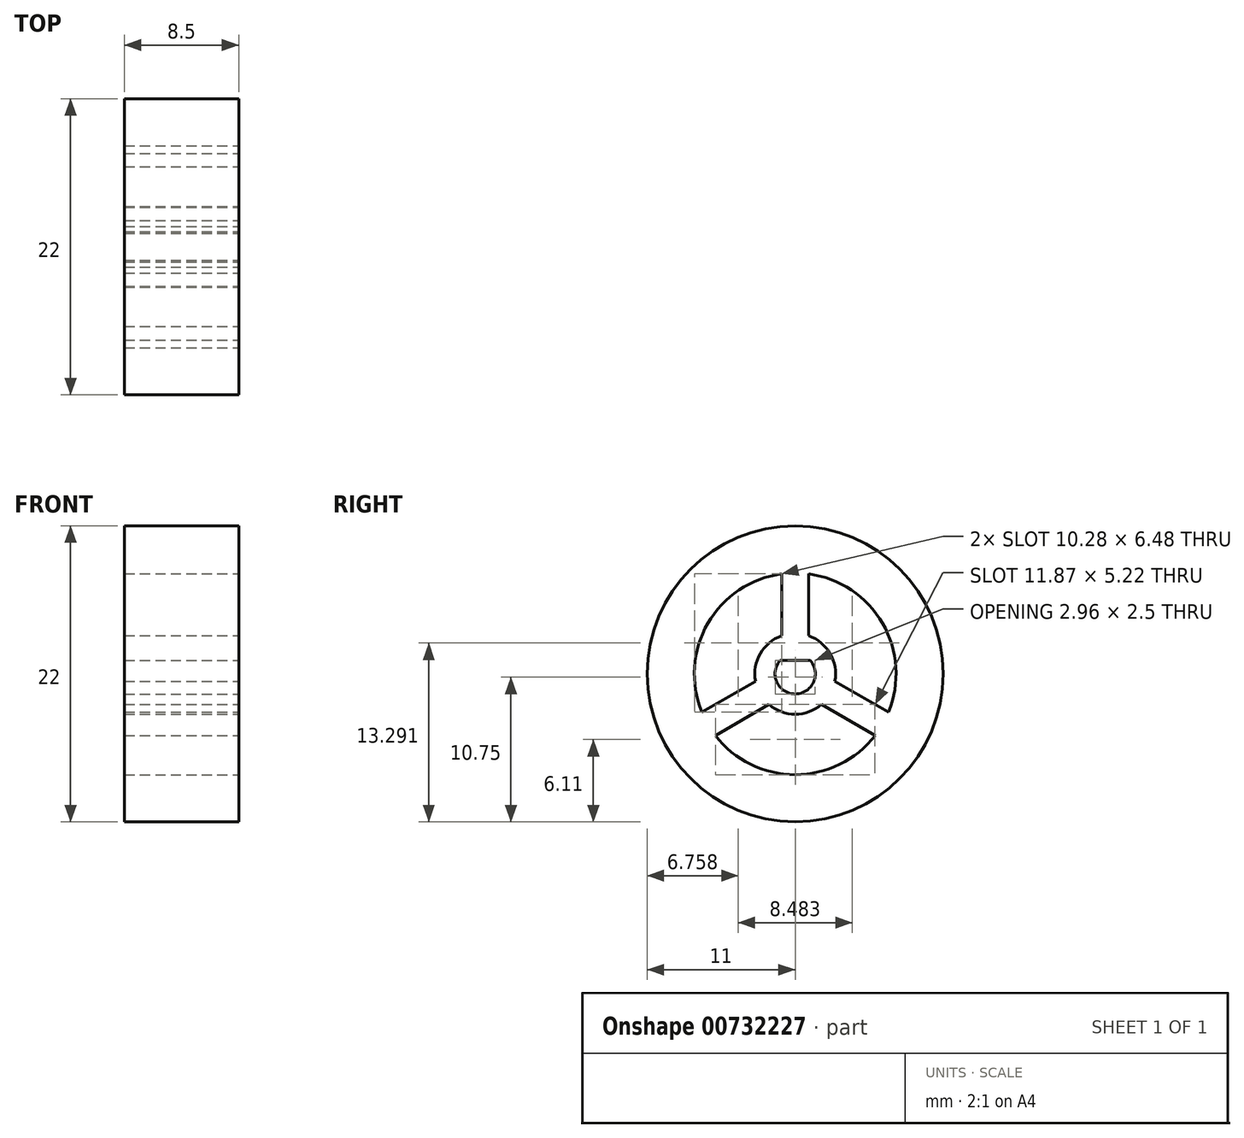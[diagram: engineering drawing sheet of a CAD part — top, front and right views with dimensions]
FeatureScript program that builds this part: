
annotation { "Feature Type Name" : "Feature", "Feature Type Description" : "" }
export const myFeature = defineFeature(function(context is Context, id is Id, definition is map)
    precondition{}
    {
        {
            var Q0;
            Q0=qCreatedBy(makeId("Right.planeOp"),FACE);
            var sketch = newSketch(context, id + "F0", { "sketchPlane" : qUnion([Q0])});
            skCircle(sketch, "E0", {"center": v(0, 0) * mm, "radius": 11 * mm});
            skSolve(sketch);
        }
        {
            var Q0;
            Q0 = qSketchRegion(id + "F0", true);
            extrude(context, id + "F1", {"entities" : qUnion([Q0]), "depth" : 8.5 * mm, "offsetDistance" : 25 * mm});
        }
        {
            var Q0;
            Q0=makeQuery(id+"F1.opExtrude","CAP_FACE",FACE,{"disambiguationData":[OSD([sQuery(id+"F0.wireOp",EDGE,"E0")])],"isStart":false});
            var sketch = newSketch(context, id + "F2", { "sketchPlane" : qUnion([Q0])});
            skArc(sketch, "E1", {"start": v(-1, 7.43) * mm, "mid": v(-6.5, 3.75) * mm, "end": v(-6.94, -2.85) * mm});
            skArc(sketch, "E2", {"start": v(-1, 2.83) * mm, "mid": v(-2.6, 1.5) * mm, "end": v(-2.95, -0.55) * mm});
            skLineSegment(sketch, "E3", {"start": v(0, 7.5) * mm, "end": v(0, 3) * mm, "construction": true});
            skLineSegment(sketch, "E4", {"start": v(0, 3) * mm, "end": v(1, 3) * mm, "construction": true});
            skLineSegment(sketch, "E5", {"start": v(1, 3) * mm, "end": v(1, 7.43) * mm});
            skLineSegment(sketch, "E6", {"start": v(1, 3) * mm, "end": v(1, 2.83) * mm});
            skLineSegment(sketch, "E7.MirrorCS", {"start": v(1, 3) * mm, "end": v(1, 3.17) * mm});
            skLineSegment(sketch, "E8.MirrorCS", {"start": v(1, 3) * mm, "end": v(1, -1.43) * mm});
            skLineSegment(sketch, "E9.MirrorCS", {"start": v(-1, 3) * mm, "end": v(-1, 7.43) * mm});
            skLineSegment(sketch, "E10.MirrorCS", {"start": v(0, 3) * mm, "end": v(-1, 3) * mm, "construction": true});
            skLineSegment(sketch, "E11.MirrorCS", {"start": v(-1, 3) * mm, "end": v(-1, 2.83) * mm});
            skLineSegment(sketch, "E12.1.0", {"start": v(-2.1, -2.37) * mm, "end": v(-5.94, -4.58) * mm});
            skLineSegment(sketch, "E12.1.1", {"start": v(-6.5, -3.75) * mm, "end": v(-2.6, -1.5) * mm, "construction": true});
            skLineSegment(sketch, "E12.1.2", {"start": v(-3.1, -0.63) * mm, "end": v(-6.94, -2.85) * mm});
            skLineSegment(sketch, "E12.1.3", {"start": v(-2.6, -1.5) * mm, "end": v(-3.1, -0.63) * mm, "construction": true});
            skLineSegment(sketch, "E12.1.4", {"start": v(-3.1, -0.63) * mm, "end": v(-2.95, -0.55) * mm});
            skLineSegment(sketch, "E12.1.5", {"start": v(-2.6, -1.5) * mm, "end": v(-2.1, -2.37) * mm, "construction": true});
            skLineSegment(sketch, "E12.1.6", {"start": v(-2.1, -2.37) * mm, "end": v(-1.95, -2.28) * mm});
            skLineSegment(sketch, "E12.2.0", {"start": v(3.1, -0.63) * mm, "end": v(6.94, -2.85) * mm});
            skLineSegment(sketch, "E12.2.1", {"start": v(6.5, -3.75) * mm, "end": v(2.6, -1.5) * mm, "construction": true});
            skLineSegment(sketch, "E12.2.2", {"start": v(2.1, -2.37) * mm, "end": v(5.94, -4.58) * mm});
            skLineSegment(sketch, "E12.2.3", {"start": v(2.6, -1.5) * mm, "end": v(2.1, -2.37) * mm, "construction": true});
            skLineSegment(sketch, "E12.2.4", {"start": v(2.1, -2.37) * mm, "end": v(1.95, -2.28) * mm});
            skLineSegment(sketch, "E12.2.5", {"start": v(2.6, -1.5) * mm, "end": v(3.1, -0.63) * mm, "construction": true});
            skLineSegment(sketch, "E12.2.6", {"start": v(3.1, -0.63) * mm, "end": v(2.95, -0.55) * mm});
            skArc(sketch, "E13.trimOffspring", {"start": v(2.95, -0.55) * mm, "mid": v(2.6, 1.5) * mm, "end": v(1, 2.83) * mm});
            skArc(sketch, "E14.trimOffspring", {"start": v(6.94, -2.85) * mm, "mid": v(6.5, 3.75) * mm, "end": v(1, 7.43) * mm});
            skArc(sketch, "E15.trimOffspring", {"start": v(-1.95, -2.28) * mm, "mid": v(0, -3) * mm, "end": v(1.95, -2.28) * mm});
            skArc(sketch, "E16.trimOffspring", {"start": v(-5.94, -4.58) * mm, "mid": v(0, -7.5) * mm, "end": v(5.94, -4.58) * mm});
            skSolve(sketch);
        }
        {
            var Q0;
            Q0=makeQuery(id+"F2.imprint","IMPRINT",FACE,{"disambiguationData":[TD([[makeQuery(id+"F2.imprint","IMPRINT",EDGE,{"derivedFrom":sQuery(id+"F2.wireOp",EDGE,"E1")}),1.0]])]});
            var Q1;
            Q1=makeQuery(id+"F2.imprint","IMPRINT",FACE,{"disambiguationData":[TD([[makeQuery(id+"F2.imprint","IMPRINT",EDGE,{"derivedFrom":sQuery(id+"F2.wireOp",EDGE,"E5")}),-1.0]])]});
            var Q2;
            Q2=makeQuery(id+"F2.imprint","IMPRINT",FACE,{"disambiguationData":[TD([[makeQuery(id+"F2.imprint","IMPRINT",EDGE,{"derivedFrom":sQuery(id+"F2.wireOp",EDGE,"E12.1.0")}),1.0]])]});
            var Q3;
            Q3=makeQuery(id+"F1.opExtrude","CAP_FACE",FACE,{"disambiguationData":[OSD([sQuery(id+"F0.wireOp",EDGE,"E0")])],"isStart":true});
            extrude(context, id + "F3", {"entities" : qUnion([Q0, Q1, Q2]), "operationType" : NewBodyOperationType.REMOVE, "endBound" : BoundingType.UP_TO_SURFACE, "oppositeDirection" : true, "depth" : 25 * mm, "endBoundEntityFace" : qUnion([Q3]), "offsetDistance" : 25 * mm});
        }
        {
            var Q0;
            Q0=makeQuery(id+"F1.opExtrude","CAP_FACE",FACE,{"disambiguationData":[OSD([sQuery(id+"F0.wireOp",EDGE,"E0")])],"isStart":false});
            var sketch = newSketch(context, id + "F4", { "sketchPlane" : qUnion([Q0])});
            skArc(sketch, "E17", {"start": v(-1.12, 1) * mm, "mid": v(0, -1.5) * mm, "end": v(1.12, 1) * mm});
            skLineSegment(sketch, "E18", {"start": v(-1.12, 1) * mm, "end": v(1.12, 1) * mm});
            skSolve(sketch);
        }
        {
            var Q0;
            Q0=makeQuery(id+"F4.imprint","IMPRINT",FACE,{"disambiguationData":[TD([[makeQuery(id+"F4.imprint","IMPRINT",EDGE,{"derivedFrom":sQuery(id+"F4.wireOp",EDGE,"E17")}),1.0]])]});
            var Q1;
            Q1=makeQuery(id+"F1.opExtrude","CAP_FACE",FACE,{"disambiguationData":[OSD([sQuery(id+"F0.wireOp",EDGE,"E0")])],"isStart":true});
            extrude(context, id + "F5", {"entities" : qUnion([Q0]), "operationType" : NewBodyOperationType.REMOVE, "endBound" : BoundingType.UP_TO_SURFACE, "oppositeDirection" : true, "depth" : 25 * mm, "endBoundEntityFace" : qUnion([Q1]), "offsetDistance" : 25 * mm});
        }
    });
